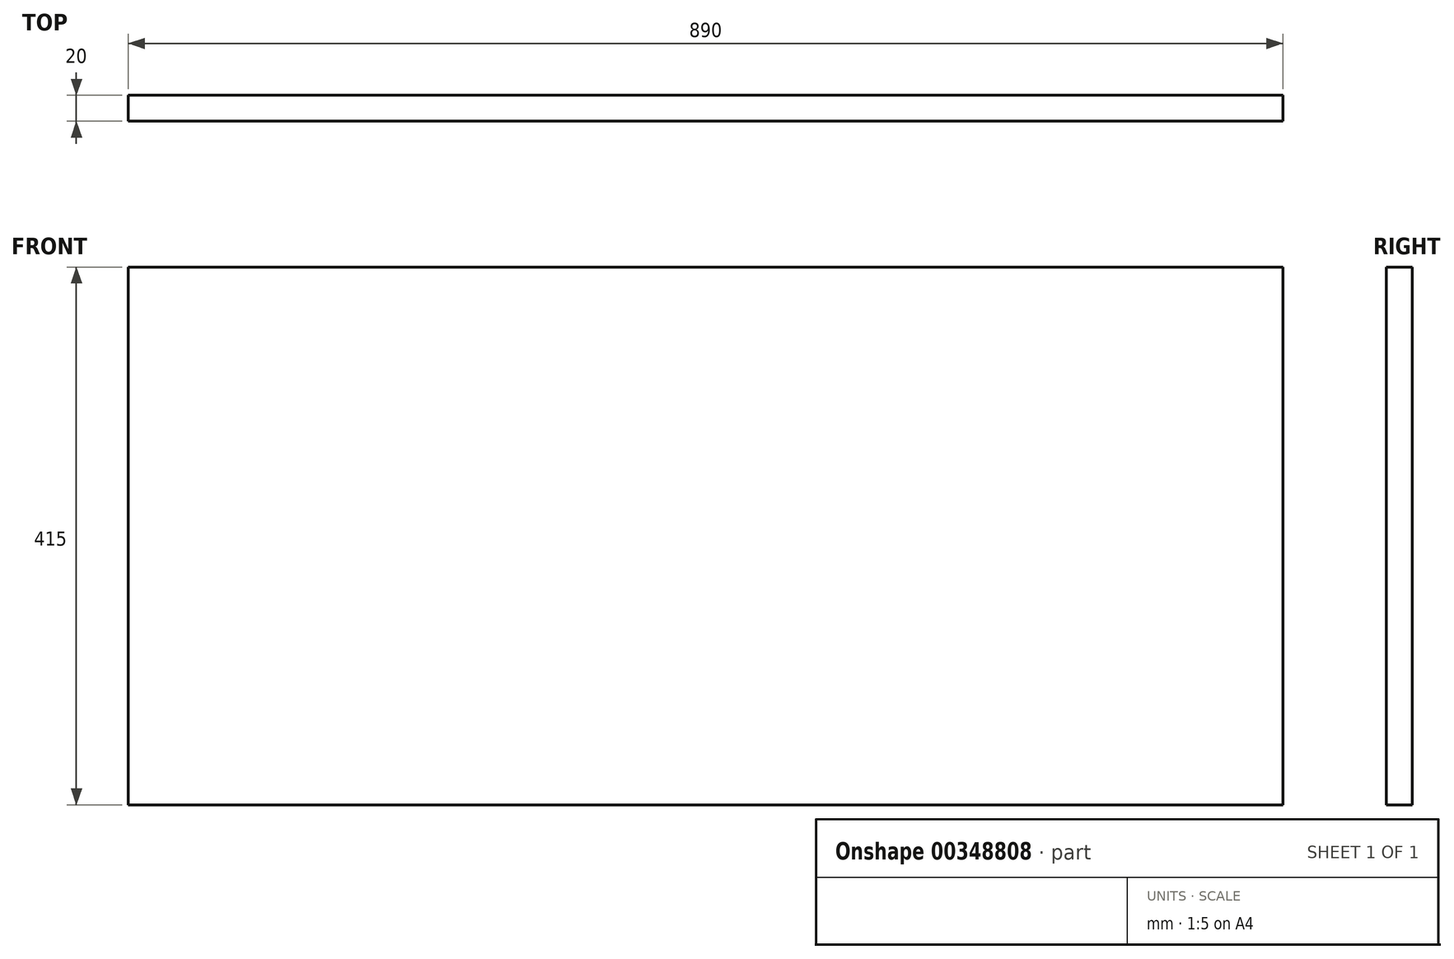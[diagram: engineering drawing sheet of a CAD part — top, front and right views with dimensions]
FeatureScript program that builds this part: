
annotation { "Feature Type Name" : "Feature", "Feature Type Description" : "" }
export const myFeature = defineFeature(function(context is Context, id is Id, definition is map)
    precondition{}
    {
        {
            var Q0;
            Q0=qCreatedBy(makeId("Front.planeOp"),FACE);
            var sketch = newSketch(context, id + "F0", { "sketchPlane" : qUnion([Q0])});
            skLineSegment(sketch, "E0.bottom", {"start": v(-890, -415) * mm, "end": v(0, -415) * mm});
            skLineSegment(sketch, "E0.top", {"start": v(-890, 0) * mm, "end": v(0, 0) * mm});
            skLineSegment(sketch, "E0.left", {"start": v(-890, -415) * mm, "end": v(-890, 0) * mm});
            skLineSegment(sketch, "E0.right", {"start": v(0, -415) * mm, "end": v(0, 0) * mm});
            skSolve(sketch);
        }
        {
            var Q0;
            Q0=qSketchRegion(id+"F0",true);
            extrude(context, id + "F1", {"entities" : qUnion([Q0]), "depth" : 20 * mm});
        }
    });
